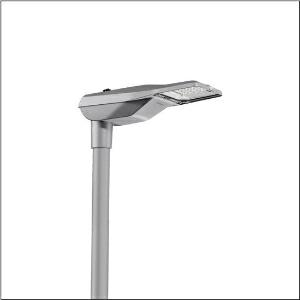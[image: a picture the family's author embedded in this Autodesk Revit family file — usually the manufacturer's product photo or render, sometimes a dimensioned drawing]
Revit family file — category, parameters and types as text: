
# Revit family: streetlight_sl_21_iq_micro___p0_8a_5xe1u31v08db_560e
name_source: partatom
category: Lighting Fixtures
units: mm (PartAtom-declared; Revit-internal decimal feet)

## family parameters
Cut with Voids When Loaded = No
Host = Face
Light Source = No
Part Type = Normal
Room Calculation Point = No
Round Connector Dimension = Use Diameter
Shared = No

## types (1)
- --- (1 x LED, 5130 lm, 39.1 W, 3000K)
    Apparent Load = 39 VA
    CIE Flux Codes = 33 69 96 100 100
    Color Rendering = 70
    Color Temperature = 3000K
    Default Elevation = 1800 mm
    Description = Streetlight SL 21 iQ micro, mast luminaire, primary light control with lens, of PMMA, primary optical cover: cover, of toughened safety glass, transparent, light distribution: P0.8a, light emission: direct distribution, primary light characteristic: asymmetric, installation type: post-top, side-entry, LED, High Power LED, rated luminous flux: 5.130lm, luminous efficacy: 131lm/W, light colour: 730, colour temperature: 3000K, control gear: iQ-Street Remote, D4i with power reduction, control: pre-setting: logarithmic dimming characteristic, Street-Remote, Auto-Match, Temp-Guard, Lumen-Switch, Night-Set, Smart-Wire, Light-Fading, Desk-Remote (wireless, voltage-free reading and setting of iQ features in the workshop via application-optimized NFC function/RFID function), optimised constant luminous flux control (CLO 2.0), mains connection: 220..240V, AC, 50/60Hz, start of lifetime: 39W, end of service life: 41W, reduction: 17W, luminaire housing, of diecast aluminium, powder-coated, Siteco® metallic grey (DB 702S), corrosivity category C5 high according to DIN EN ISO 12944, please order mast flange separately, inclination adjustable: 0°, 5°, 10°, 15°, sealing non-destructively replaceable, multi-level sealing system, length: 528mm, width: 235mm, height: 110mm, mast flange for spigot size: 42mm (side-entry): 5XC10008XM4, 60/48mm (side-entry/post-top): 5XC10108XM2, 76/60mm (side-entry/post-top): 5XC10108XM1, mounting height: 4..8m, Smart Interface above, protection rating (complete): IP66, insulation class (complete): insulation class II (safety insulation), certification: CE, ENEC, ENEC+, VDE, impact resistance: IK10, permissible operating ambient temperature for outdoor applications: -40..+50°C, standard-compliant lighting for roads and squares, packaging unit: 1 piece

Light Distribution: P0.8a
    Height = 110 mm
    Lamp = 1 x LED
    Lamp Light Flux = 5130 lm
    Lamp Power = 39.1 W
    Lamp count = 1
    Length = 528 mm
    Luminous efficacy = 131 lm/W
    Manufacturer = Siteco
    ModVariant = No
    Model = 5XE1U31V08DB
    Number of Poles = 1
    OnlyDefault = Yes
    Power Factor = 1
    Product Name = Streetlight SL 21 iQ micro | P0.8a
    Product group = mast luminaire | pylon top
    ProductGroupID = 6100
    Protection Class = Protection class II
    Protection Degree = IP 66
    RLX_Detail_Level = 1
    RLX_Emergency_Light_Flux = 0 lm
    RLX_Emergency_Type = 0
    RLX_Emergency_Type_DB = No
    RlxData = <blob elided: 98161 chars, md5=831a06af>
    Socket = socket
    Standby Power = 0 W
    System Light Flux = 5130 lm
    System Power = 39 W
    Type Comments = factory setting: luminous flux: 100 % | dim-lin: 254 | 765 mA
    Type Image = l_1277292.jpg
    URL = http://relux.com
    VarID = @adj_084713
    Voltage = 0 V
    Weight = 0.00 kg
    Width = 235 mm

## geometry (parser evidence)
native form markers: Blend x4, Sweep x9
no freeform markers — native parametric forms only
